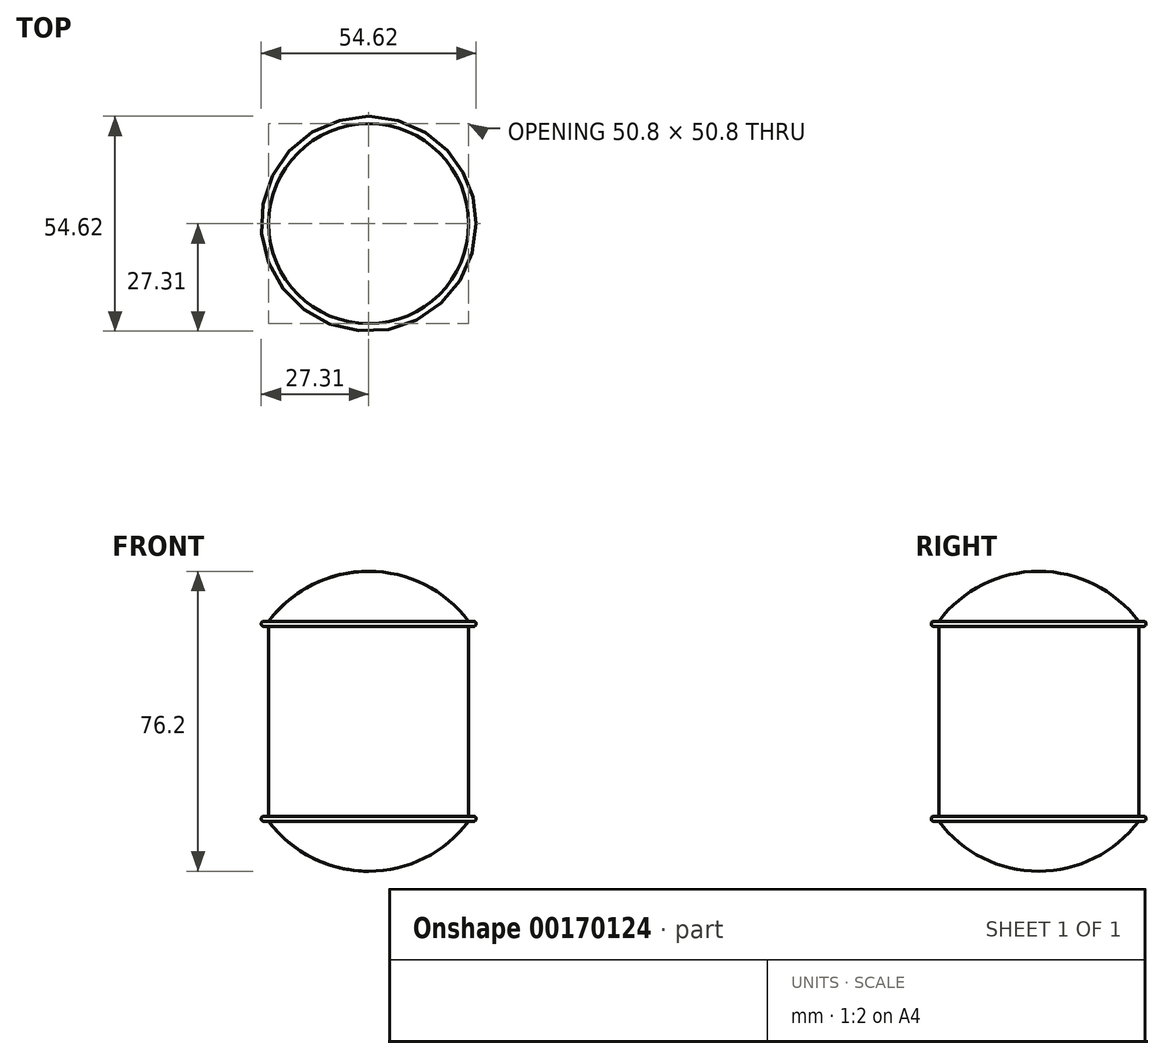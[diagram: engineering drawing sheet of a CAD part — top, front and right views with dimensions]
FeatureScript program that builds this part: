
annotation { "Feature Type Name" : "Feature", "Feature Type Description" : "" }
export const myFeature = defineFeature(function(context is Context, id is Id, definition is map)
    precondition{}
    {
        {
            var Q0;
            Q0=qCreatedBy(makeId("Front.planeOp"),FACE);
            var sketch = newSketch(context, id + "F0", { "sketchPlane" : qUnion([Q0])});
            skLineSegment(sketch, "E0", {"start": v(-25.4, 0) * mm, "end": v(-25.4, 24.13) * mm});
            skArc(sketch, "E1", {"start": v(0, 38.1) * mm, "mid": v(-14.2, 34.75) * mm, "end": v(-25.4, 25.4) * mm});
            skLineSegment(sketch, "E2", {"start": v(-25.4, 25.4) * mm, "end": v(-26.67, 25.4) * mm});
            skLineSegment(sketch, "E3", {"start": v(-26.67, 24.13) * mm, "end": v(-25.4, 24.13) * mm});
            skArc(sketch, "E4", {"start": v(-26.67, 25.4) * mm, "mid": v(-27.3, 24.77) * mm, "end": v(-26.67, 24.13) * mm});
            skLineSegment(sketch, "E5.MirrorCS", {"start": v(-25.4, -25.4) * mm, "end": v(-26.67, -25.4) * mm});
            skArc(sketch, "E6.MirrorCS", {"start": v(-26.67, -25.4) * mm, "mid": v(-27.3, -24.77) * mm, "end": v(-26.67, -24.13) * mm});
            skLineSegment(sketch, "E7.MirrorCS", {"start": v(-26.67, -24.13) * mm, "end": v(-25.4, -24.13) * mm});
            skArc(sketch, "E8.MirrorCS", {"start": v(0, -38.1) * mm, "mid": v(-14.2, -34.75) * mm, "end": v(-25.4, -25.4) * mm});
            skLineSegment(sketch, "E9.MirrorCS", {"start": v(-25.4, 0) * mm, "end": v(-25.4, -24.13) * mm});
            skLineSegment(sketch, "E10", {"start": v(0, 55.8) * mm, "end": v(0, -59.4) * mm});
            skSolve(sketch);
        }
        {
            var Q0;
            Q0=makeQuery(id+"F0.imprint","IMPRINT",FACE,{"disambiguationData":[TD([[makeQuery(id+"F0.imprint","IMPRINT",EDGE,{"derivedFrom":sQuery(id+"F0.wireOp",EDGE,"E0")}),-1.0]])]});
            var Q1;
            Q1=sQuery(id+"F0.wireOp",EDGE,"E10");
            revolve(context, id + "F1", {"entities" : qUnion([Q0]), "axis" : qUnion([Q1]), "revolveType" : RevolveType.FULL});
        }
    });
